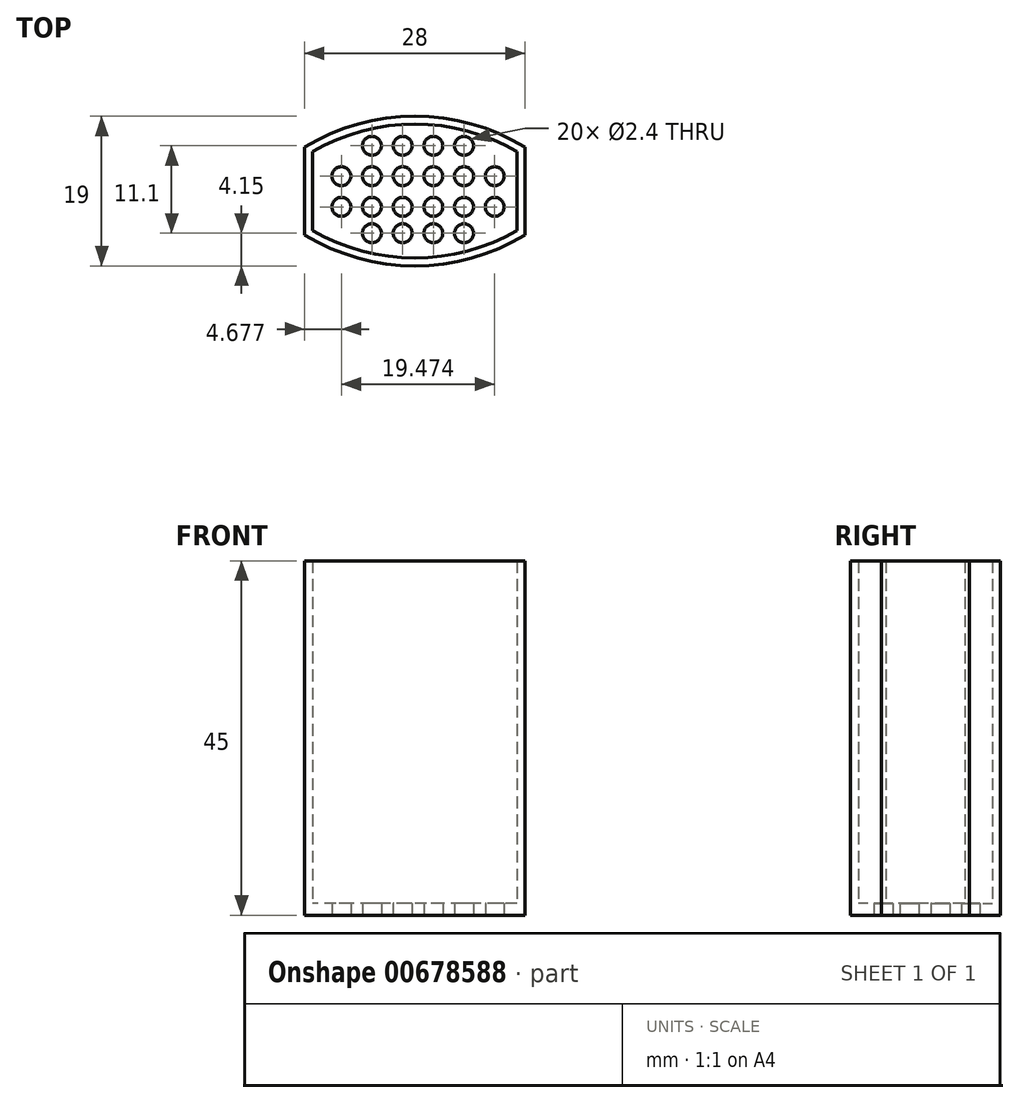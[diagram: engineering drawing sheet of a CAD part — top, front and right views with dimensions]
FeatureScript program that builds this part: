
annotation { "Feature Type Name" : "Feature", "Feature Type Description" : "" }
export const myFeature = defineFeature(function(context is Context, id is Id, definition is map)
    precondition{}
    {
        {
            var Q0;
            Q0=qCreatedBy(makeId("Top.planeOp"),FACE);
            var sketch = newSketch(context, id + "F0", { "sketchPlane" : qUnion([Q0])});
            skLineSegment(sketch, "E0", {"start": v(-40.38, -5.94) * mm, "end": v(-40.38, -15.94) * mm});
            skLineSegment(sketch, "E1", {"start": v(-14.38, -5.94) * mm, "end": v(-14.38, -15.94) * mm});
            skArc(sketch, "E2", {"start": v(-14.38, -5.94) * mm, "mid": v(-27.38, -2.44) * mm, "end": v(-40.38, -5.94) * mm});
            skArc(sketch, "E3", {"start": v(-40.38, -15.94) * mm, "mid": v(-27.38, -19.44) * mm, "end": v(-14.38, -15.94) * mm});
            skArc(sketch, "E4.0", {"start": v(-13.38, -5.37) * mm, "mid": v(-27.38, -1.44) * mm, "end": v(-41.38, -5.37) * mm});
            skLineSegment(sketch, "E4.1", {"start": v(-13.38, -5.37) * mm, "end": v(-13.38, -16.5) * mm});
            skArc(sketch, "E4.2", {"start": v(-41.38, -16.5) * mm, "mid": v(-27.38, -20.44) * mm, "end": v(-13.38, -16.5) * mm});
            skLineSegment(sketch, "E4.3", {"start": v(-41.38, -5.37) * mm, "end": v(-41.38, -16.5) * mm});
            skCircle(sketch, "E5", {"center": v(-32.83, -5.2) * mm, "radius": 1.2 * mm});
            skCircle(sketch, "E6", {"center": v(-28.93, -5.2) * mm, "radius": 1.2 * mm});
            skCircle(sketch, "E7", {"center": v(-25.03, -5.2) * mm, "radius": 1.2 * mm});
            skCircle(sketch, "E8", {"center": v(-21.13, -5.2) * mm, "radius": 1.2 * mm});
            skCircle(sketch, "E9", {"center": v(-36.7, -9.05) * mm, "radius": 1.2 * mm});
            skCircle(sketch, "E10", {"center": v(-32.83, -9.05) * mm, "radius": 1.2 * mm});
            skCircle(sketch, "E11", {"center": v(-28.93, -9.05) * mm, "radius": 1.2 * mm});
            skCircle(sketch, "E12", {"center": v(-25.03, -9.05) * mm, "radius": 1.2 * mm});
            skCircle(sketch, "E13", {"center": v(-21.13, -9.05) * mm, "radius": 1.2 * mm});
            skCircle(sketch, "E14", {"center": v(-36.7, -12.95) * mm, "radius": 1.2 * mm});
            skCircle(sketch, "E15", {"center": v(-32.83, -12.95) * mm, "radius": 1.2 * mm});
            skCircle(sketch, "E16", {"center": v(-28.93, -12.95) * mm, "radius": 1.2 * mm});
            skCircle(sketch, "E17", {"center": v(-25.03, -12.95) * mm, "radius": 1.2 * mm});
            skCircle(sketch, "E18", {"center": v(-21.13, -12.95) * mm, "radius": 1.2 * mm});
            skCircle(sketch, "E19", {"center": v(-32.83, -16.3) * mm, "radius": 1.2 * mm});
            skCircle(sketch, "E20", {"center": v(-28.93, -16.3) * mm, "radius": 1.2 * mm});
            skCircle(sketch, "E21", {"center": v(-25.03, -16.3) * mm, "radius": 1.2 * mm});
            skCircle(sketch, "E22", {"center": v(-21.13, -16.3) * mm, "radius": 1.2 * mm});
            skCircle(sketch, "E23", {"center": v(-17.23, -9.05) * mm, "radius": 1.2 * mm});
            skCircle(sketch, "E24", {"center": v(-17.23, -12.95) * mm, "radius": 1.2 * mm});
            skSolve(sketch);
        }
        {
            var Q0;
            Q0=makeQuery(id+"F0.imprint","IMPRINT",FACE,{"disambiguationData":[TD([[makeQuery(id+"F0.imprint","IMPRINT",EDGE,{"derivedFrom":sQuery(id+"F0.wireOp",EDGE,"E4.0")}),1.0]])]});
            extrude(context, id + "F1", {"entities" : qUnion([Q0]), "depth" : 45 * mm, "offsetDistance" : 25 * mm});
        }
        {
            var Q0;
            Q0=makeQuery(id+"F0.imprint","IMPRINT",FACE,{"disambiguationData":[TD([[makeQuery(id+"F0.imprint","IMPRINT",EDGE,{"derivedFrom":sQuery(id+"F0.wireOp",EDGE,"E0")}),1.0]])]});
            extrude(context, id + "F2", {"entities" : qUnion([Q0]), "operationType" : NewBodyOperationType.ADD, "depth" : 1.5 * mm, "offsetDistance" : 25 * mm});
        }
    });
